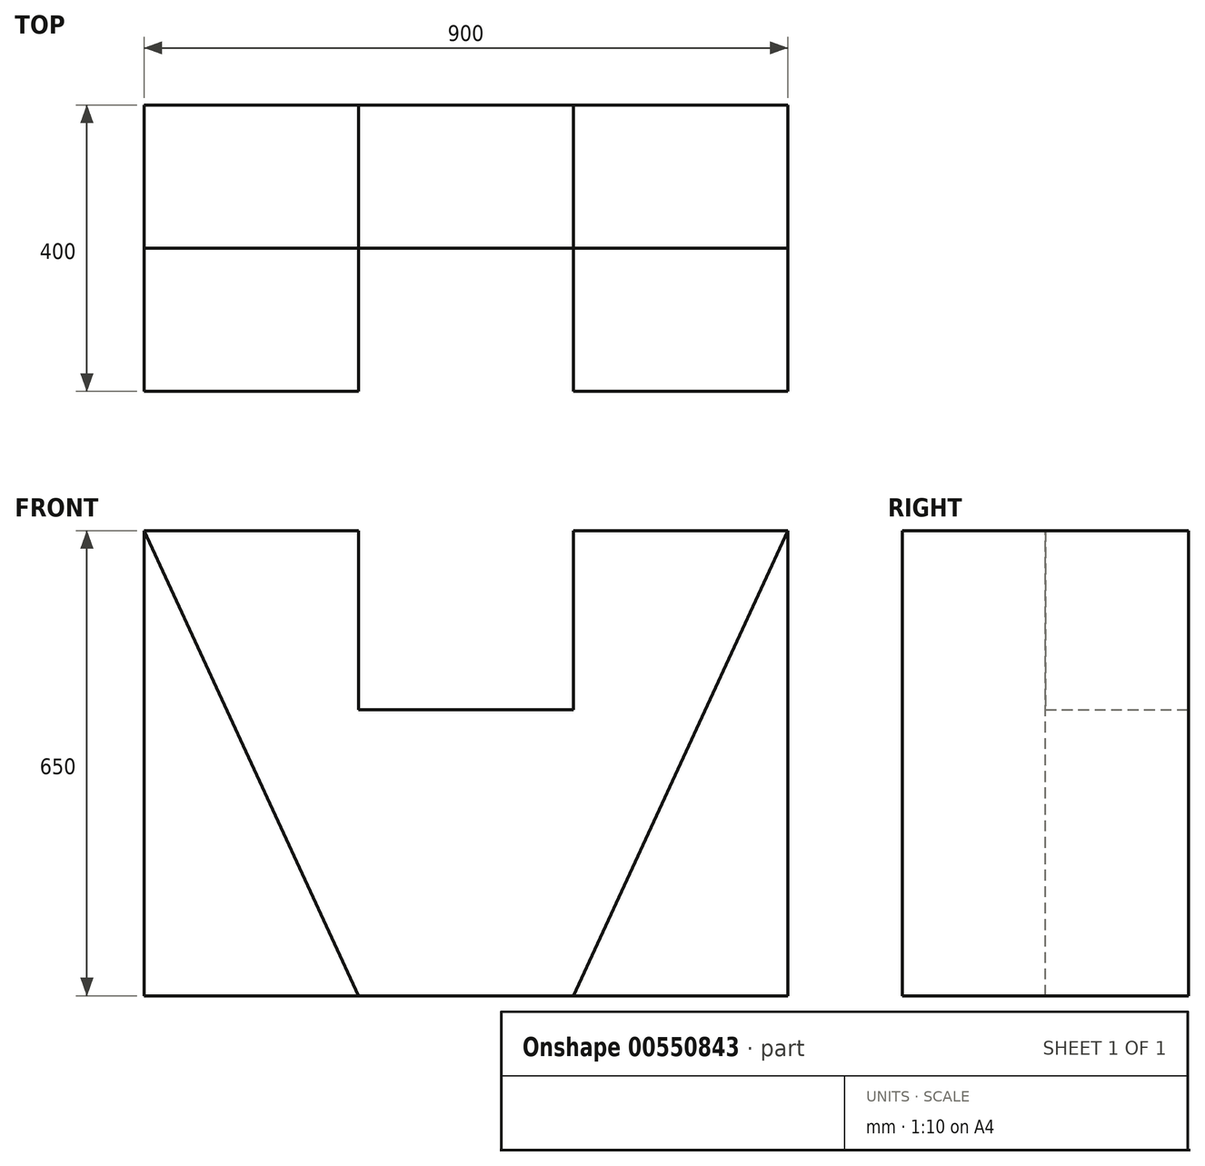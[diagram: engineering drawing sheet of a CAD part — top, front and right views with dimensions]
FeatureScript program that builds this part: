
annotation { "Feature Type Name" : "Feature", "Feature Type Description" : "" }
export const myFeature = defineFeature(function(context is Context, id is Id, definition is map)
    precondition{}
    {
        {
            var Q0;
            Q0=qCreatedBy(makeId("Front.planeOp"),FACE);
            var sketch = newSketch(context, id + "F0", { "sketchPlane" : qUnion([Q0])});
            skLineSegment(sketch, "E0.bottom", {"start": v(400.46, -350.48) * mm, "end": v(-499.54, -350.48) * mm});
            skLineSegment(sketch, "E0.top", {"start": v(400.46, 299.52) * mm, "end": v(100.46, 299.52) * mm});
            skLineSegment(sketch, "E0.left", {"start": v(400.46, -350.48) * mm, "end": v(400.46, 299.52) * mm});
            skLineSegment(sketch, "E0.right", {"start": v(-499.54, -350.48) * mm, "end": v(-499.54, 299.52) * mm});
            skPoint(sketch, "E0.middle", {"position": v(-49.54, -25.48) * mm});
            skLineSegment(sketch, "E1.top", {"start": v(-199.54, 49.52) * mm, "end": v(100.46, 49.52) * mm});
            skLineSegment(sketch, "E1.left", {"start": v(-199.54, 299.52) * mm, "end": v(-199.54, 49.52) * mm});
            skLineSegment(sketch, "E1.right", {"start": v(100.46, 299.52) * mm, "end": v(100.46, 49.52) * mm});
            skPoint(sketch, "E1.middle", {"position": v(-49.54, 299.52) * mm});
            skPoint(sketch, "E2.orphan", {"position": v(-199.54, 549.52) * mm});
            skPoint(sketch, "E3.orphan", {"position": v(100.46, 549.52) * mm});
            skLineSegment(sketch, "E4.trimOffspring", {"start": v(-199.54, 299.52) * mm, "end": v(-499.54, 299.52) * mm});
            skSolve(sketch);
        }
        {
            var Q0;
            Q0=makeQuery(id+"F0.imprint","IMPRINT",FACE,{"disambiguationData":[TD([[makeQuery(id+"F0.imprint","IMPRINT",EDGE,{"derivedFrom":sQuery(id+"F0.wireOp",EDGE,"E0.bottom")}),-1.0]])]});
            extrude(context, id + "F1", {"entities" : qUnion([Q0]), "depth" : 200 * mm, "offsetDistance" : 25.4 * mm});
        }
        {
            var Q0;
            Q0=makeQuery(id+"F1.opExtrude","CAP_FACE",FACE,{"disambiguationData":[OSD([sQuery(id+"F0.wireOp",EDGE,"E0.bottom"),sQuery(id+"F0.wireOp",EDGE,"E0.top"),sQuery(id+"F0.wireOp",EDGE,"E0.left"),sQuery(id+"F0.wireOp",EDGE,"E0.right"),sQuery(id+"F0.wireOp",EDGE,"E1.top"),sQuery(id+"F0.wireOp",EDGE,"E1.left"),sQuery(id+"F0.wireOp",EDGE,"E1.right"),sQuery(id+"F0.wireOp",EDGE,"E4.trimOffspring")])],"isStart":false});
            var sketch = newSketch(context, id + "F2", { "sketchPlane" : qUnion([Q0])});
            skLineSegment(sketch, "E5", {"start": v(-499.54, -350.48) * mm, "end": v(-199.54, -350.48) * mm});
            skLineSegment(sketch, "E6", {"start": v(-199.54, -350.48) * mm, "end": v(-499.54, 299.52) * mm});
            skLineSegment(sketch, "E7", {"start": v(400.46, -350.48) * mm, "end": v(100.46, -350.48) * mm});
            skLineSegment(sketch, "E8", {"start": v(100.46, -350.48) * mm, "end": v(400.46, 299.52) * mm});
            skSolve(sketch);
        }
        {
            var Q0;
            Q0 = qSketchRegion(id + "F2", true);
            var Q1;
            Q1=makeQuery(id+"F2.imprint","IMPRINT",FACE,{"disambiguationData":[TD([[makeQuery(id+"F2.imprint","IMPRINT",EDGE,{"derivedFrom":sQuery(id+"F2.wireOp",EDGE,"E5")}),-1.0]])]});
            var Q2;
            Q2=makeQuery(id+"F2.imprint","IMPRINT",FACE,{"disambiguationData":[TD([[makeQuery(id+"F2.imprint","IMPRINT",EDGE,{"derivedFrom":sQuery(id+"F2.wireOp",EDGE,"E7")}),-1.0]])]});
            extrude(context, id + "F3", {"entities" : qUnion([Q0, Q1, Q2]), "operationType" : NewBodyOperationType.ADD, "depth" : 200 * mm, "offsetDistance" : 25.4 * mm});
        }
    });
